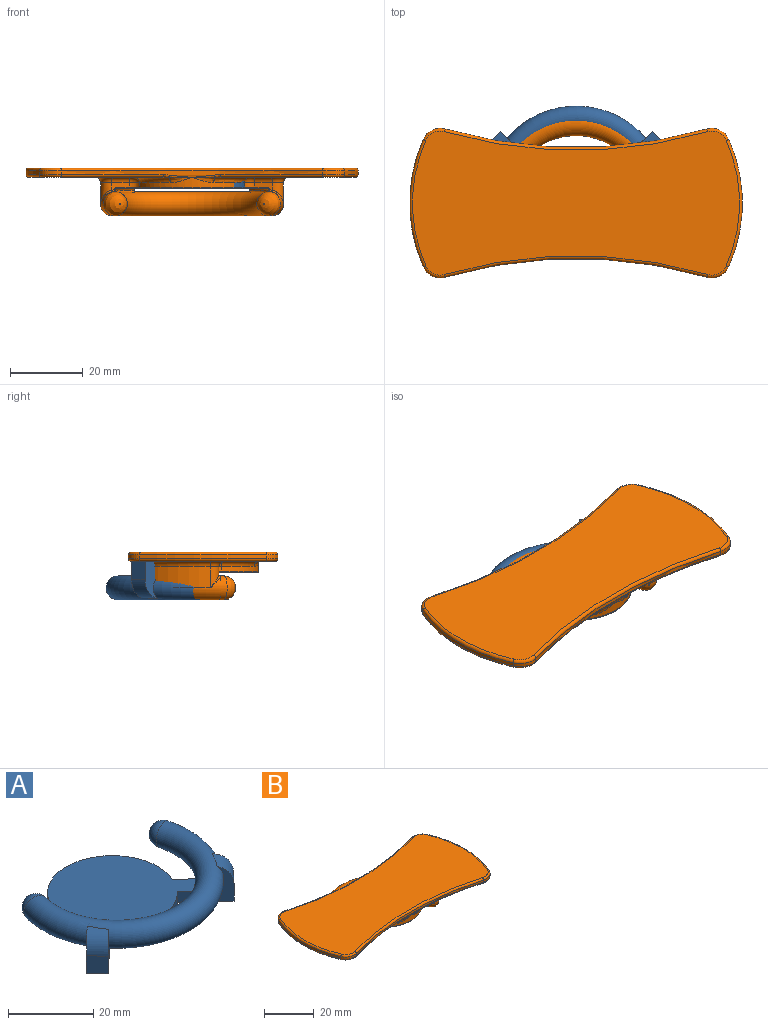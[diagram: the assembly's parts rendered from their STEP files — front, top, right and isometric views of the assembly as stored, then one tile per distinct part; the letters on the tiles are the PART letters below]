
ASSEMBLY  parts=2 mates=1
PART A: 17 faces, bbox 54.6x43.9x10.7 mm
  f0: cylinder r=15.24mm len=22.29mm, axis (0,0,-1), area 76.2mm2, adj f2,f3,f5,f7
  f1: cylinder r=15.24mm len=30.48mm, axis (0,0,-1), area 184.1mm2, adj f2,f3,f4,f6
  f2: plane 40.15x30.73mm, normal (0,0,1), area 808.5mm2, adj f0,f1,f4,f5,f6,f7,f8,f12
  f3: plane 48.79x34.76mm, normal (0,0,-1), area 868.5mm2, adj f0,f1,f4,f5,f6,f7,f10,f14
  f4: plane 10.42x10.16mm, normal (0.68,0.73,0), area 67.4mm2, adj f1,f2,f3,f8,f9,f10,f11
  f5: plane 10.11x9.86mm, normal (-0.68,-0.73,0), area 60.3mm2, adj f0,f2,f3,f8,f9,f10,f11
  f6: plane 10.42x10.16mm, normal (-0.68,0.73,0), area 67.4mm2, adj f1,f2,f3,f11,f12,f13,f14
  f7: plane 10.11x9.86mm, normal (0.68,-0.73,0), area 60.3mm2, adj f0,f2,f3,f11,f12,f13,f14
  f8: plane 3.72x3.47mm, normal (-0.73,0.68,0), area 5mm2, adj f2,f4,f5,f11
  f9: cylinder r=5.08mm len=7.08mm, axis (0.68,0.73,0), area 36.9mm2, adj f4,f5,f10,f11
  f10: plane 5.08x3.72mm, normal (0.73,-0.68,0), area 25.8mm2, adj f3,f4,f5,f9
  f11: torus R=21.87mm, axis (0,0,-1), area 1575.5mm2, adj f4,f5,f6,f7,f8,f9,f12,f13
  f12: plane 3.72x3.47mm, normal (0.73,0.68,0), area 5mm2, adj f2,f6,f7,f11
  f13: cylinder r=5.08mm len=7.08mm, axis (-0.68,0.73,0), area 36.9mm2, adj f6,f7,f11,f14
  f14: plane 5.08x3.72mm, normal (-0.73,-0.68,0), area 25.8mm2, adj f3,f6,f7,f13
  f15: sphere r=3.3mm, area 68.5mm2, adj f11
  f16: sphere r=3.3mm, area 68.5mm2, adj f11
PART B: 164 faces, bbox 98.6x48.2x13.2 mm
  f0: plane 6.11x2.41mm, normal (0,0,-1), area 7mm2, adj f82,f83,f84,f139
  f1: plane 39.59x36.95mm, normal (0,0,-1), area 811.6mm2, adj f72,f74,f76,f78,f79,f80,f144,f145
  f2: plane 41.71x29.72mm, normal (0,0,-1), area 714.2mm2, adj f25,f26,f27,f28,f29,f30,f31,f32
  f3: cylinder r=15.24mm len=28.78mm, axis (0,0,1), area 52.4mm2, adj f60,f64,f70,f72,f92,f93,f108
  f4: torus R=21.87mm, axis (0,0,1), area 1406.3mm2, adj f8,f9,f11,f17,f56,f58,f112,f113
  f5: cylinder r=15.24mm len=19.09mm, axis (0,0,1), area 33mm2, adj f61,f65,f68,f69,f81,f82,f98
  f6: plane 0.25x0.24mm, normal (-0.4,-0.92,0), area 0.1mm2, adj f9
  f7: plane 0.25x0.24mm, normal (0.4,-0.92,0), area 0.1mm2, adj f8
  f8: bspline ~7.09x6.68mm, area 67.3mm2, adj f4,f7
  f9: bspline ~7.08x6.68mm, area 67.3mm2, adj f4,f6
  f10: cylinder r=21.36mm len=18mm, axis (0,0,-1), area 1.2mm2, adj f58,f59,f94,f107
  f11: cylinder r=25.17mm len=16.99mm, axis (0,0,-1), area 104.1mm2, adj f4,f66,f67,f80
  f12: plane 4.8x2.01mm, normal (0.19,-0.98,0), area 6.4mm2, adj f64,f67,f76,f109,f111,f113
  f13: plane 3.58x3.34mm, normal (0.68,0.73,0), area 6.4mm2, adj f65,f66,f73,f75,f95,f96,f117
  f14: cylinder r=21.36mm len=18mm, axis (0,0,-1), area 1.2mm2, adj f56,f57,f102,f103
  f15: plane 4.8x2.01mm, normal (-0.19,-0.98,0), area 6.4mm2, adj f60,f63,f90,f104,f105,f121
  f16: plane 3.58x3.34mm, normal (-0.68,0.73,0), area 6.4mm2, adj f61,f62,f84,f85,f100,f101,f125
  f17: cylinder r=25.17mm len=16.99mm, axis (0,0,-1), area 104.1mm2, adj f4,f62,f63,f88
  f18: plane 6.11x2.41mm, normal (0,0,-1), area 7mm2, adj f69,f71,f73,f153
  f19: plane 39.59x36.95mm, normal (0,0,-1), area 811.6mm2, adj f87,f88,f89,f90,f91,f92,f130,f131
  f20: cylinder r=43.18mm len=35.09mm, axis (0,0,-1), area 36.7mm2, adj f54,f55,f132,f159
  f21: cylinder r=128.75mm len=71.87mm, axis (0,0,-1), area 84mm2, adj f52,f54,f134,f135,f136,f137,f138,f139
  f22: cylinder r=43.18mm len=35.09mm, axis (0,0,-1), area 36.7mm2, adj f52,f53,f146,f160
  f23: cylinder r=128.75mm len=71.87mm, axis (0,0,-1), area 80.1mm2, adj f53,f55,f128,f129,f130,f142,f143,f144
  f24: plane 89.92x39.59mm, normal (0,0,1), area 2905.4mm2, adj f156,f157,f158,f159,f160,f161,f162,f163
  f25: extruded ~3.09x2.07mm, area 2.9mm2, adj f2,f26,f50,f51
  f26: plane 8.54x0.76mm, normal (-1,0,0), area 6.5mm2, adj f2,f25,f27,f51
  f27: plane 7.14x0.76mm, normal (0,1,0), area 5.4mm2, adj f2,f26,f28,f51
  f28: plane 2.37x0.76mm, normal (1,0,0), area 1.8mm2, adj f2,f27,f29,f51
  f29: plane 3.91x0.76mm, normal (0.04,-1,0), area 3mm2, adj f2,f28,f30,f51
  f30: plane 5.22x0.76mm, normal (1,0,0), area 4mm2, adj f2,f29,f31,f51
  f31: extruded ~2x0.9mm, area 1.7mm2, adj f2,f30,f32,f51
  f32: extruded ~3.19x0.76mm, area 2.5mm2, adj f2,f31,f33,f51
  f33: extruded ~5.57x2.63mm, area 4.9mm2, adj f2,f32,f34,f51
  f34: extruded ~6.91x2.02mm, area 5.6mm2, adj f2,f33,f35,f51
  f35: plane 0.76x0.42mm, normal (-1,0,0), area 0.3mm2, adj f2,f34,f36,f51
  f36: extruded ~6.85x2.08mm, area 5.6mm2, adj f2,f35,f37,f51
  f37: extruded ~5.95x2.64mm, area 5.1mm2, adj f2,f36,f38,f51
  f38: extruded ~2.72x0.76mm, area 2.1mm2, adj f2,f37,f39,f51
  f39: extruded ~1.94x1.08mm, area 1.7mm2, adj f2,f38,f40,f51
  f40: plane 3.29x0.79mm, normal (0.97,-0.23,0), area 2.6mm2, adj f2,f39,f41,f51
  f41: plane 2.26x0.76mm, normal (0,-1,0), area 1.7mm2, adj f2,f40,f42,f51
  f42: plane 4.32x0.76mm, normal (-1,0,0), area 3.3mm2, adj f2,f41,f43,f51
  f43: extruded ~3.38x2.18mm, area 3.1mm2, adj f2,f42,f44,f51
  f44: extruded ~4.66x0.83mm, area 3.6mm2, adj f2,f43,f45,f51
  f45: extruded ~7.94x3.34mm, area 6.8mm2, adj f2,f44,f46,f51
  f46: extruded ~8.72x2.99mm, area 7.2mm2, adj f2,f45,f47,f51
  f47: plane 0.76x0.39mm, normal (1,0,0), area 0.3mm2, adj f2,f46,f48,f51
  f48: extruded ~8.71x3.02mm, area 7.2mm2, adj f2,f47,f49,f51
  f49: extruded ~7.8x3.36mm, area 6.7mm2, adj f2,f48,f50,f51
  f50: extruded ~5.32x0.97mm, area 4.2mm2, adj f2,f25,f49,f51
  f51: plane 24.52x19.23mm, normal (0,0,-1), area 178mm2, adj f25,f26,f27,f28,f29,f30,f31,f32
  f52: cylinder r=5.08mm len=6.06mm, axis (0,0,1), area 7.4mm2, adj f21,f22,f147,f162
  f53: cylinder r=5.08mm len=6.06mm, axis (0,0,1), area 7.4mm2, adj f22,f23,f145,f158
  f54: cylinder r=5.08mm len=6.06mm, axis (0,0,1), area 7.4mm2, adj f20,f21,f133,f161
  f55: cylinder r=5.08mm len=6.06mm, axis (0,0,1), area 7.4mm2, adj f20,f23,f131,f157
  f56: torus R=20.85mm, axis (0,0,-1), area 12.7mm2, adj f4,f14,f122,f127
  f57: torus R=20.85mm, axis (0,0,1), area 15.3mm2, adj f2,f14,f101,f104
  f58: torus R=20.85mm, axis (0,0,-1), area 12.7mm2, adj f4,f10,f115,f118
  f59: torus R=20.85mm, axis (0,0,1), area 15.3mm2, adj f2,f10,f95,f109
  f60: cylinder r=2.54mm len=2.88mm, axis (0,0,1), area 4.1mm2, adj f3,f15,f91,f106
  f61: cylinder r=2.54mm len=3.32mm, axis (0,0,1), area 4.1mm2, adj f5,f16,f83,f99
  f62: cylinder r=2.54mm len=5.79mm, axis (0,0,-1), area 15mm2, adj f16,f17,f86,f87,f124
  f63: cylinder r=2.54mm len=5.77mm, axis (0,0,-1), area 16.6mm2, adj f15,f17,f89,f120
  f64: cylinder r=2.54mm len=2.88mm, axis (0,0,1), area 4.1mm2, adj f3,f12,f74,f110
  f65: cylinder r=2.54mm len=3.32mm, axis (0,0,1), area 4.1mm2, adj f5,f13,f71,f97
  f66: cylinder r=2.54mm len=5.79mm, axis (0,0,-1), area 15mm2, adj f11,f13,f77,f79,f116
  f67: cylinder r=2.54mm len=5.77mm, axis (0,0,-1), area 16.6mm2, adj f11,f12,f78,f112
  f68: bspline ~6.91x1.67mm, area 3.6mm2, adj f5,f69,f155
  f69: torus R=16.76mm, axis (0,0,1), area 9.8mm2, adj f5,f18,f68,f71,f154
  f70: bspline ~6.91x1.67mm, area 3.6mm2, adj f3,f72,f142
  f71: torus R=1.02mm, axis (0,0,1), area 6.8mm2, adj f18,f65,f69,f73
  f72: torus R=16.76mm, axis (0,0,1), area 31mm2, adj f1,f3,f70,f74,f143
  f73: cylinder r=1.52mm len=4.26mm, axis (0.73,-0.68,0), area 10.1mm2, adj f13,f18,f71,f75,f152
  f74: torus R=1.02mm, axis (0,0,1), area 6.8mm2, adj f1,f64,f72,f76
  f75: bspline ~1.58x1.56mm, area 0.7mm2, adj f13,f73,f77,f151
  f76: cylinder r=1.52mm len=5.09mm, axis (-0.98,-0.19,0), area 11.7mm2, adj f1,f12,f74,f78
  f77: bspline ~5.57x1.84mm, area 4.3mm2, adj f66,f75,f79,f150
  f78: torus R=4.06mm, axis (0,0,1), area 12.5mm2, adj f1,f67,f76,f80
  f79: torus R=4.06mm, axis (0,0,1), area 2.2mm2, adj f1,f66,f77,f80,f149
  f80: torus R=26.7mm, axis (0,0,1), area 44.2mm2, adj f1,f11,f78,f79
  f81: bspline ~6.91x1.67mm, area 3.6mm2, adj f5,f82,f140
  f82: torus R=16.76mm, axis (0,0,1), area 9.8mm2, adj f0,f5,f81,f83,f141
  f83: torus R=1.02mm, axis (0,0,1), area 6.8mm2, adj f0,f61,f82,f84
  f84: cylinder r=1.52mm len=4.26mm, axis (-0.73,-0.68,0), area 10.1mm2, adj f0,f16,f83,f85,f138
  f85: bspline ~1.58x1.56mm, area 0.7mm2, adj f16,f84,f86,f137
  f86: bspline ~5.58x1.9mm, area 4.7mm2, adj f62,f85,f87,f136
  f87: torus R=4.06mm, axis (0,0,1), area 2.2mm2, adj f19,f62,f86,f88,f135
  f88: torus R=26.7mm, axis (0,0,1), area 44.2mm2, adj f17,f19,f87,f89
  f89: torus R=4.06mm, axis (0,0,1), area 12.5mm2, adj f19,f63,f88,f90
  f90: cylinder r=1.52mm len=5.09mm, axis (0.98,-0.19,0), area 11.7mm2, adj f15,f19,f89,f91
  f91: torus R=1.02mm, axis (0,0,1), area 6.8mm2, adj f19,f60,f90,f92
  f92: torus R=16.76mm, axis (0,0,1), area 31mm2, adj f3,f19,f91,f93,f129
  f93: bspline ~6.91x1.67mm, area 4.6mm2, adj f3,f92,f128
  f94: cylinder r=0.38mm len=0.27mm, axis (0,0,-1), area 0mm2, adj f10,f95,f118
  f95: bspline ~1.09x0.91mm, area 0.6mm2, adj f13,f59,f94,f96,f119
  f96: cylinder r=0.38mm len=2.64mm, axis (-0.73,0.68,0), area 1.9mm2, adj f2,f13,f95,f97
  f97: torus R=2.92mm, axis (0,0,1), area 2.3mm2, adj f2,f65,f96,f98
  f98: torus R=14.86mm, axis (0,0,1), area 12.2mm2, adj f2,f5,f97,f99
  f99: torus R=2.92mm, axis (0,0,1), area 2.3mm2, adj f2,f61,f98,f100
  f100: cylinder r=0.38mm len=2.64mm, axis (0.73,0.68,0), area 1.9mm2, adj f2,f16,f99,f101
  f101: bspline ~0.96x0.94mm, area 0.6mm2, adj f16,f57,f100,f102,f126
  f102: cylinder r=0.38mm len=0.27mm, axis (0,0,-1), area 0mm2, adj f14,f101,f127
  f103: cylinder r=0.38mm len=0.28mm, axis (0,0,-1), area 0mm2, adj f14,f104,f122
  f104: bspline ~1.07x0.94mm, area 0.6mm2, adj f15,f57,f103,f105,f123
  f105: cylinder r=0.38mm len=3.27mm, axis (-0.98,0.19,0), area 1.9mm2, adj f2,f15,f104,f106
  f106: torus R=2.92mm, axis (0,0,1), area 2.3mm2, adj f2,f60,f105,f108
  f107: cylinder r=0.38mm len=0.28mm, axis (0,0,-1), area 0mm2, adj f10,f109,f115
  f108: torus R=14.86mm, axis (0,0,1), area 22.3mm2, adj f2,f3,f106,f110
  f109: bspline ~1.09x1.07mm, area 0.6mm2, adj f12,f59,f107,f111,f114
  f110: torus R=2.92mm, axis (0,0,1), area 2.3mm2, adj f2,f64,f108,f111
  f111: cylinder r=0.38mm len=3.27mm, axis (0.98,0.19,0), area 1.9mm2, adj f2,f12,f109,f110
  f112: bspline ~3.81x3.66mm, area 1.6mm2, adj f4,f67,f113
  f113: bspline ~1.41x0.73mm, area 0.6mm2, adj f4,f12,f112,f114
  f114: bspline ~0.68x0.65mm, area 0.3mm2, adj f4,f109,f113,f115
  f115: bspline ~0.88x0.57mm, area 0.3mm2, adj f4,f58,f107,f114
  f116: bspline ~4.18x3.76mm, area 1.6mm2, adj f4,f66,f117
  f117: bspline ~1.3x1.24mm, area 0.6mm2, adj f4,f13,f116,f119
  f118: bspline ~0.81x0.6mm, area 0.3mm2, adj f4,f58,f94,f119
  f119: bspline ~0.7x0.59mm, area 0.3mm2, adj f4,f95,f117,f118
  f120: bspline ~3.76x3.2mm, area 1.6mm2, adj f4,f63,f121
  f121: bspline ~1.38x0.74mm, area 0.6mm2, adj f4,f15,f120,f123
  f122: bspline ~0.88x0.57mm, area 0.3mm2, adj f4,f56,f103,f123
  f123: bspline ~0.67x0.61mm, area 82.7mm2, adj f4,f104,f121,f122
  f124: bspline ~4.5x3.81mm, area 1.6mm2, adj f4,f62,f125
  f125: bspline ~1.33x1.21mm, area 0.6mm2, adj f4,f16,f124,f126
  f126: bspline ~0.75x0.62mm, area 0.3mm2, adj f4,f101,f125,f127
  f127: bspline ~0.81x0.6mm, area 0.3mm2, adj f4,f56,f102,f126
  f128: bspline ~6.79x0.86mm, area 1.9mm2, adj f23,f93,f129
  f129: bspline ~4.45x1.1mm, area 1.8mm2, adj f23,f92,f128,f130
  f130: torus R=129.51mm, axis (0,0,1), area 34.1mm2, adj f19,f23,f129,f131
  f131: torus R=4.32mm, axis (0,0,1), area 8.3mm2, adj f19,f55,f130,f132
  f132: torus R=42.42mm, axis (0,0,1), area 43mm2, adj f19,f20,f131,f133
  f133: torus R=4.32mm, axis (0,0,1), area 8.3mm2, adj f19,f54,f132,f134
  f134: torus R=129.51mm, axis (0,0,1), area 18.3mm2, adj f19,f21,f133,f135
  f135: bspline ~2.48x1.05mm, area 1.3mm2, adj f21,f87,f134,f136
  f136: bspline ~4.31x0.97mm, area 4.8mm2, adj f21,f86,f135,f137
  f137: bspline ~0.77x0.71mm, area 0.3mm2, adj f21,f85,f136,f138
  f138: bspline ~2.53x1.15mm, area 1.6mm2, adj f21,f84,f137,f139
  f139: torus R=129.51mm, axis (0,0,1), area 7.3mm2, adj f0,f21,f138,f141
  f140: bspline ~6.38x0.79mm, area 2.8mm2, adj f21,f81,f141
  f141: bspline ~3.84x1.1mm, area 1.8mm2, adj f21,f82,f139,f140
  f142: bspline ~6.38x0.79mm, area 2.8mm2, adj f23,f70,f143
  f143: bspline ~4.45x1.1mm, area 1.8mm2, adj f23,f72,f142,f144
  f144: torus R=129.51mm, axis (0,0,1), area 34.1mm2, adj f1,f23,f143,f145
  f145: torus R=4.32mm, axis (0,0,1), area 8.3mm2, adj f1,f53,f144,f146
  f146: torus R=42.42mm, axis (0,0,1), area 43mm2, adj f1,f22,f145,f147
  f147: torus R=4.32mm, axis (0,0,1), area 8.3mm2, adj f1,f52,f146,f148
  f148: torus R=129.51mm, axis (0,0,1), area 18.3mm2, adj f1,f21,f147,f149
  f149: bspline ~2.48x1.05mm, area 1.3mm2, adj f21,f79,f148,f150
  f150: bspline ~4.35x1.06mm, area 2.5mm2, adj f21,f77,f149,f151
  f151: bspline ~0.8x0.79mm, area 0.3mm2, adj f21,f75,f150,f152
  f152: bspline ~2.27x1.05mm, area 1.6mm2, adj f21,f73,f151,f153
  f153: torus R=129.51mm, axis (0,0,1), area 7.3mm2, adj f18,f21,f152,f154
  f154: bspline ~3.84x1.1mm, area 1.8mm2, adj f21,f69,f153,f155
  f155: bspline ~6.79x0.86mm, area 1.9mm2, adj f21,f68,f154
  f156: torus R=129.51mm, axis (0,0,1), area 87.4mm2, adj f23,f24,f157,f158
  f157: torus R=4.32mm, axis (0,0,1), area 8.3mm2, adj f24,f55,f156,f159
  f158: torus R=4.32mm, axis (0,0,1), area 8.3mm2, adj f24,f53,f156,f160
  f159: torus R=42.42mm, axis (0,0,1), area 43mm2, adj f20,f24,f157,f161
  f160: torus R=42.42mm, axis (0,0,1), area 43mm2, adj f22,f24,f158,f162
  f161: torus R=4.32mm, axis (0,0,1), area 8.3mm2, adj f24,f54,f159,f163
  f162: torus R=4.32mm, axis (0,0,1), area 8.3mm2, adj f24,f52,f160,f163
  f163: torus R=129.51mm, axis (0,0,1), area 87.4mm2, adj f21,f24,f161,f162
PLACE A rot(axis=(1,0,0),180deg) t=(0.11,5.72,-15.88)mm
PLACE B at identity fixed
MATE fastened A.f2 <-> B.f2  axis (0,0,-1) through (0.11,1.19,-13.59)mm
